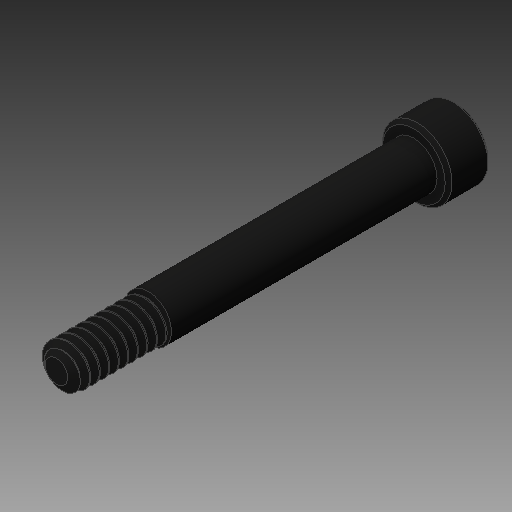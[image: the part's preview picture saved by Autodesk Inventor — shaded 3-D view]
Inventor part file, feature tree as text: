
AUTODESK INVENTOR PART (.ipt)
format: ipt  version: 2018 (Build 220112000, 112)  size: 532,992 bytes
history: native  units: in
note: dims shown in document units (in); Inventor stores cm internally (conversion verified against a paired STEP export)
features: chamfer x1
ambient origin geometry x8: Origin, YZ Plane, XZ Plane, XY Plane, X Axis, Y Axis, Z Axis, Center Point
bodies: Solid1 (feature_tree)
feature tree (1):
  chamfer  "Chamfer1"  [1 undecoded]
note: 1 required parameter value undecoded (feature->parameter linkage not recoverable at this tier; creation-order binding heuristic only, values carry confidence <= 0.55)
